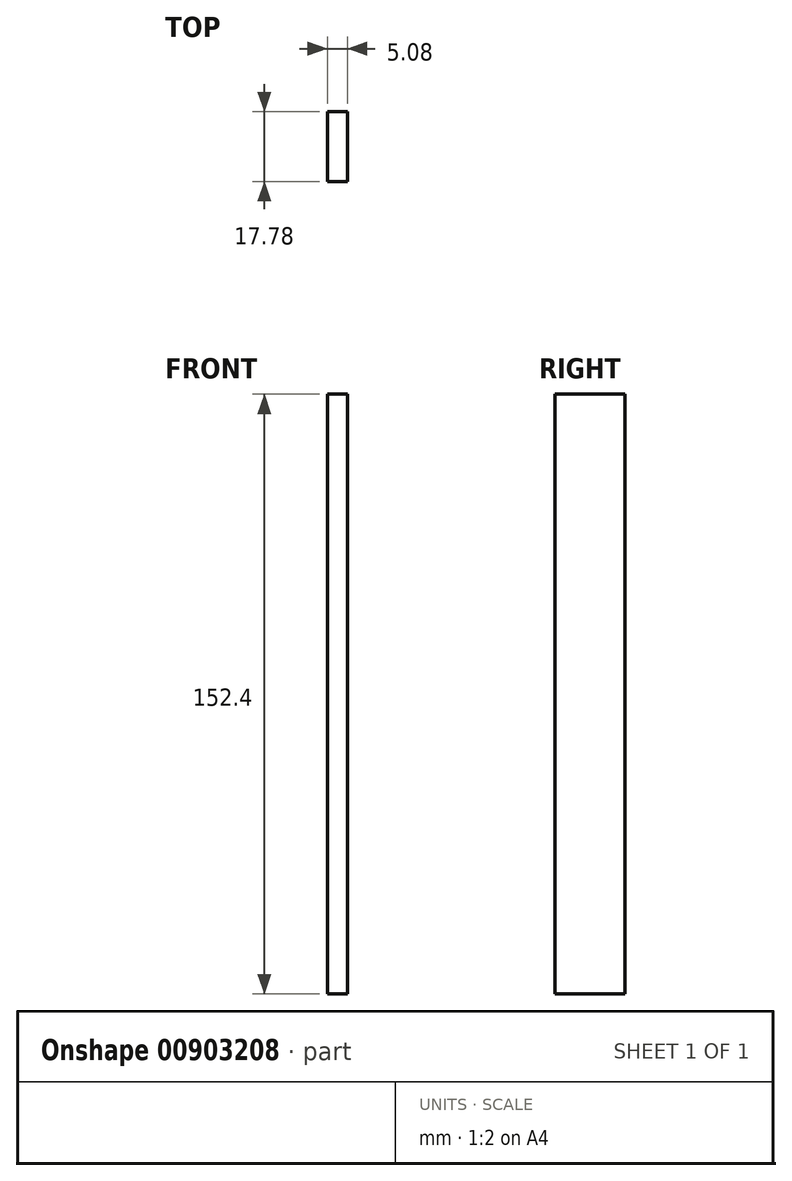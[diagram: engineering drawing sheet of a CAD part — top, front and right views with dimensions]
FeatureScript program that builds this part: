
annotation { "Feature Type Name" : "Feature", "Feature Type Description" : "" }
export const myFeature = defineFeature(function(context is Context, id is Id, definition is map)
    precondition{}
    {
        {
            var Q0;
            Q0=qCreatedBy(makeId("Front.planeOp"),FACE);
            var sketch = newSketch(context, id + "F0", { "sketchPlane" : qUnion([Q0])});
            skLineSegment(sketch, "E0.bottom", {"start": v(-43.97, 107.35) * mm, "end": v(-38.9, 107.35) * mm});
            skLineSegment(sketch, "E0.top", {"start": v(-43.97, -45.05) * mm, "end": v(-38.9, -45.05) * mm});
            skLineSegment(sketch, "E0.left", {"start": v(-43.97, 107.35) * mm, "end": v(-43.97, -45.05) * mm});
            skLineSegment(sketch, "E0.right", {"start": v(-38.9, 107.35) * mm, "end": v(-38.9, -45.05) * mm});
            skSolve(sketch);
        }
        {
            var Q0;
            Q0 = qSketchRegion(id + "F0", true);
            extrude(context, id + "F1", {"entities" : qUnion([Q0]), "depth" : 17.78 * mm, "offsetDistance" : 25.4 * mm});
        }
    });
